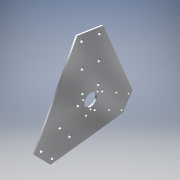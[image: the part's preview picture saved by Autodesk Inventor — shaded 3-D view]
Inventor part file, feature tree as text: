
AUTODESK INVENTOR PART (.ipt)
format: ipt  version: 2019 (Build 230136000, 136)  size: 218,624 bytes
history: native  units: in
note: dims shown in document units (in); Inventor stores cm internally (conversion verified against a paired STEP export)
features: extrude x3, sketch x3, chamfer x1, fillet x1, pattern_circular x1
ambient origin geometry x8: Origin, YZ Plane, XZ Plane, XY Plane, X Axis, Y Axis, Z Axis, Center Point
bodies: Body1 (feature_tree)
feature tree (9):
  extrude  "Extrusion2"  Depth=8.0in
  extrude  "Extrusion3"  Depth=0.125in
  extrude  "Extrusion4"  Depth=0.125in TaperAngle=360.0deg
  chamfer  "Chamfer1"  Distance=1.1547in
  fillet  "Fillet1"  Radius=1.125in
  pattern_circular  "Circular Pattern1"  [2 undecoded]
  sketch  "Sketch1"  dims[d0=8.0in d1=2.0in]
  sketch  "Sketch2"  dims[d2=0.25in d4=0.125in]
  sketch  "Sketch3"  dims[d7=0.7in d8=1.1811in d10=360.0deg d14=1.1547in d15=1.125in d16=0.125in d17=0.0in d18=1.25in d19=30.0deg d20=0.25in d21=1.1811in d23=360.0deg d25=0.21in d26=1.1811in d28=360.0deg d30=0.25in d31=0.0in d32=3.5in d33=0.2996in d34=0.125in d35=0.25in d36=0.125in d37=0.25in d38=0.25in d39=0.25in d40=0.25in d41=0.0in d42=0.125in d43=0.125in d44=45.0deg d45=0.0312in d46=1.1811in d47=360.0deg]
note: 2 required parameter values undecoded (feature->parameter linkage not recoverable at this tier; creation-order binding heuristic only, values carry confidence <= 0.55)
